# Revit family: Faucet-Bath-KALLISTA-002-P34127-1
name_source: partatom
category: Plumbing Fixtures
units: mm (PartAtom-declared; Revit-internal decimal feet)

## family parameters
Cut with Voids When Loaded = No
Host = Face
OmniClass Number = 23.31.11.00
OmniClass Title = Faucets
Part Type = Normal
Room Calculation Point = No
Round Connector Dimension = Use Diameter
Shared = No

## types (5) — shared parameters
ADA Compliant = No
Assembly Code = D2010
CW Connection = Yes
Cold Water Inlet = Cold Water Inlet
Date Modified = 11/29/2023
Default Elevation = 914.4 mm  [stored 3 ft]
Description = Capsule Freestanding Bath Faucet Handle
Drain Included = No
Flow Rate = 7 GPM
HW Connection = Yes
Handle Clearance = 97.579 mm  [stored 0.320141 ft]
Height = 969.863 mm
Hot Water Inlet = Hot Water Inlet
Length = 273.248 mm
Manufacturer = Kallista Co.
Master Format 2014 = 22 41 39
Master Format 2014 Name = Residential Faucets, Supplies, and Trim
Material = Premium Metal Constuction
Pressure = 60.00 psi
Product Name = 002
Spout Reach = 273.248 mm
URL = https://www.kallista.com
Vent Connection = No
Waste Connection = No
Waste Water Outlet = Waste Water Outlet
WaterSense Certified = No
Width = 124.023 mm

## per-type parameters (varying)
| type | Finish | Model | Type |
| BAF-Brushed French Gold | Kallista-Metal-BAF-Brushed_French_Gold | P34127-LV-BAF | 1 |
| BL-Matte Black | Kallista-Metal-BL-Matte_Black | P34127-LV-BL | 2 |
| BN-Brushed Nickel | Kallista-Metal-BN-Brushed_Nickel | P34127-LV-BN | 3 |
| CP-Chrome | Kallista-Metal-CP-Chrome | P34127-LV-CP | 4 |
| SN-Polished Nickel | Kallista-Metal-SN-Polished_Nickel | P34127-LV-SN | 5 |

note: [stored X ft] marks values corroborated as IEEE doubles in the binary element streams (Revit-internal decimal feet)

## geometry (parser evidence)
native form markers: Sweep x6
no freeform markers — native parametric forms only
